# Revit family: Door_Overhead-Sectional_OHD_Steel-Standard-Lift
name_source: partatom
category: Doors
units: mm (PartAtom-declared; Revit-internal decimal feet)

## family parameters
Always vertical = Yes
Classification Number = 23.30.10.17.37.14
Cut with Voids When Loaded = No
Host = Wall
Room Calculation Point = No
Shared = No

## types (18) — shared parameters
Analytic Construction = <None>
Assembly Code = B2030410
Construction Details = https://www.arcat.com
Define Thermal Properties by = Schematic Type
Fire Rating = as Specified
Function = Interior
Green Building-LEED = https://www.arcat.com
Heat Transfer Coefficient (U) = 0.1 BTU/(h·ft²·°F)
Height = 0' - 0"
Keynote = 08 36 00
Manufacturer = Overhead Door Corporation
Operation = as Specified
Product Data = http://www.arcat.com
Rough Height = 0' - 0"
Rough Width = 0' - 0"
SpecWizard = https://www.arcat.com
Specification = https://www.arcat.com
Thermal Resistance (R) = 0.0000 (h·ft²·°F)/BTU
Thickness = 0' - 0"
Type Comments = Confirm Track Requirements with Overhead Door
URL = http://www.overheaddoor.com
Wall Closure = By host
Width = 0' - 0"
zero-valued in all types: Cost, Solar Heat Gain Coefficient, Visual Light Transmittance

## per-type parameters (varying)
| type | Description | Model |
| Low Headroom Lift 432 Series | Overhead Door Corp Insulated Sectional Door - 432 Series as Specified | 432 |
| Low Headroom Lift 430 Series | Overhead Door Corp Sectional Door - 430 Series as Specified | 430 |
| Low Headroom Lift 426 Series | Overhead Door Corp Insulated Sectional Door - 426 Series as Specified | 426 |
| Low Headroom Lift 424 Series | Overhead Door Corp Sectional Door - 424 Series as Specified | 424 |
| Low Headroom Lift 422 Series | Overhead Door Corp Insulated Sectional Door - 422 Series as Specified | 422 |
| Low Headroom Lift 420 Series | Overhead Door Corp Sectional Door - 420 Series as Specified | 420 |
| Low Headroom Lift 418 Series | Overhead Door Corp Insulated Sectional Door - 418 Series as Specified | 418 |
| Low Headroom Lift 416 Series | Overhead Door Corp Sectional Door - 416 Series as Specified | 416 |
| Low Headroom Lift 470 Series | Overhead Door Corp Insulated Sectional Door - 470 Series as Specified | 470 |
| Standard Lift 432 Series | Overhead Door Corp Insulated Sectional Door - 432 Series as Specified | 432 |
| Standard Lift 430 Series | Overhead Door Corp Sectional Door - 430 Series as Specified | 430 |
| Standard Lift 426 Series | Overhead Door Corp Insulated Sectional Door - 426 Series as Specified | 426 |
| Standard Lift 424 Series | Overhead Door Corp Sectional Door - 424 Series as Specified | 424 |
| Standard Lift 422 Series | Overhead Door Corp Insulated Sectional Door - 422 Series as Specified | 422 |
| Standard Lift 420 Series | Overhead Door Corp Sectional Door - 420 Series as Specified | 420 |
| Standard Lift 418 Series | Overhead Door Corp Insulated Sectional Door - 418 Series as Specified | 418 |
| Standard Lift 416 Series | Overhead Door Corp Sectional Door - 416 Series as Specified | 416 |
| Standard Lift 470 Series | Overhead Door Corp Insulated Sectional Door - 470 Series as Specified | 470 |

## geometry (parser evidence)
native form markers: Sweep x29
no freeform markers — native parametric forms only
